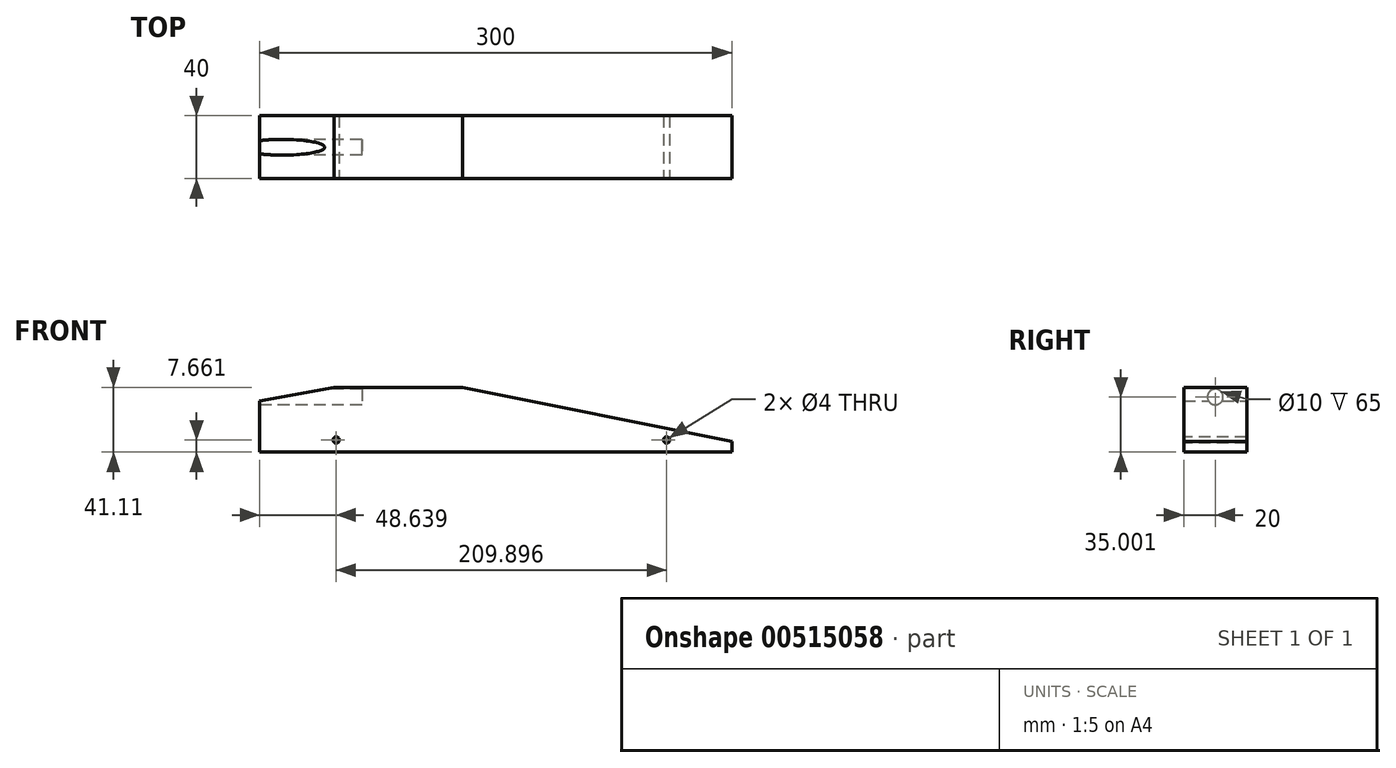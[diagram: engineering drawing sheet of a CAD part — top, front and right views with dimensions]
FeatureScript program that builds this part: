
annotation { "Feature Type Name" : "Feature", "Feature Type Description" : "" }
export const myFeature = defineFeature(function(context is Context, id is Id, definition is map)
    precondition{}
    {
        {
            var Q0;
            Q0=qCreatedBy(makeId("Front.planeOp"),FACE);
            var sketch = newSketch(context, id + "F0", { "sketchPlane" : qUnion([Q0])});
            skLineSegment(sketch, "E0.bottom", {"start": v(-84.2, -32.3) * mm, "end": v(215.8, -32.3) * mm});
            skLineSegment(sketch, "E0.top", {"start": v(-84.2, 37.7) * mm, "end": v(215.8, 37.7) * mm});
            skLineSegment(sketch, "E0.left", {"start": v(-84.2, -32.3) * mm, "end": v(-84.2, 37.7) * mm});
            skLineSegment(sketch, "E0.right", {"start": v(215.8, -32.3) * mm, "end": v(215.8, 37.7) * mm});
            skLineSegment(sketch, "E1", {"start": v(215.8, -25.69) * mm, "end": v(44.75, 8.8) * mm});
            skLineSegment(sketch, "E2", {"start": v(44.75, 8.8) * mm, "end": v(-36.94, 8.8) * mm});
            skLineSegment(sketch, "E3", {"start": v(-36.94, 8.8) * mm, "end": v(-84.2, 0) * mm});
            skSolve(sketch);
        }
        {
            var Q0;
            Q0=makeQuery(id+"F0.imprint","IMPRINT",FACE,{"disambiguationData":[TD([[makeQuery(id+"F0.imprint","IMPRINT",EDGE,{"derivedFrom":sQuery(id+"F0.wireOp",EDGE,"E0.bottom")}),1.0]])]});
            extrude(context, id + "F1", {"entities" : qUnion([Q0]), "depth" : 40 * mm});
        }
        {
            var Q0;
            Q0=makeQuery(id+"F1.opExtrude","SWEPT_FACE",FACE,{"disambiguationData":[OSD([sQuery(id+"F0.wireOp",EDGE,"E0.left")])]});
            var sketch = newSketch(context, id + "F2", { "sketchPlane" : qUnion([Q0])});
            skCircle(sketch, "E4", {"center": v(20, 2.7) * mm, "radius": 5 * mm});
            skSolve(sketch);
        }
        {
            var Q0;
            Q0=makeQuery(id+"F2.imprint","IMPRINT",FACE,{"disambiguationData":[TD([[makeQuery(id+"F2.imprint","IMPRINT",EDGE,{"derivedFrom":sQuery(id+"F2.wireOp",EDGE,"E4")}),1.0]])]});
            extrude(context, id + "F3", {"entities" : qUnion([Q0]), "operationType" : NewBodyOperationType.REMOVE, "oppositeDirection" : true, "depth" : 65 * mm});
        }
        {
            var Q0;
            Q0=makeQuery(id+"F1.opExtrude","CAP_FACE",FACE,{"disambiguationData":[OSD([sQuery(id+"F0.wireOp",EDGE,"E0.bottom"),sQuery(id+"F0.wireOp",EDGE,"E0.top"),sQuery(id+"F0.wireOp",EDGE,"E0.left"),sQuery(id+"F0.wireOp",EDGE,"E0.right")])],"isStart":false});
            var sketch = newSketch(context, id + "F4", { "sketchPlane" : qUnion([Q0])});
            skCircle(sketch, "E5", {"center": v(-35.56, -24.64) * mm, "radius": 2 * mm});
            skCircle(sketch, "E6", {"center": v(174.33, -24.64) * mm, "radius": 2 * mm});
            skSolve(sketch);
        }
        {
            var Q0;
            Q0=makeQuery(id+"F4.imprint","IMPRINT",FACE,{"disambiguationData":[TD([[makeQuery(id+"F4.imprint","IMPRINT",EDGE,{"derivedFrom":sQuery(id+"F4.wireOp",EDGE,"E5")}),1.0]])]});
            var Q1;
            Q1=makeQuery(id+"F4.imprint","IMPRINT",FACE,{"disambiguationData":[TD([[makeQuery(id+"F4.imprint","IMPRINT",EDGE,{"derivedFrom":sQuery(id+"F4.wireOp",EDGE,"E6")}),1.0]])]});
            extrude(context, id + "F5", {"entities" : qUnion([Q0, Q1]), "operationType" : NewBodyOperationType.REMOVE, "endBound" : BoundingType.THROUGH_ALL, "oppositeDirection" : true, "depth" : 25 * mm});
        }
    });
